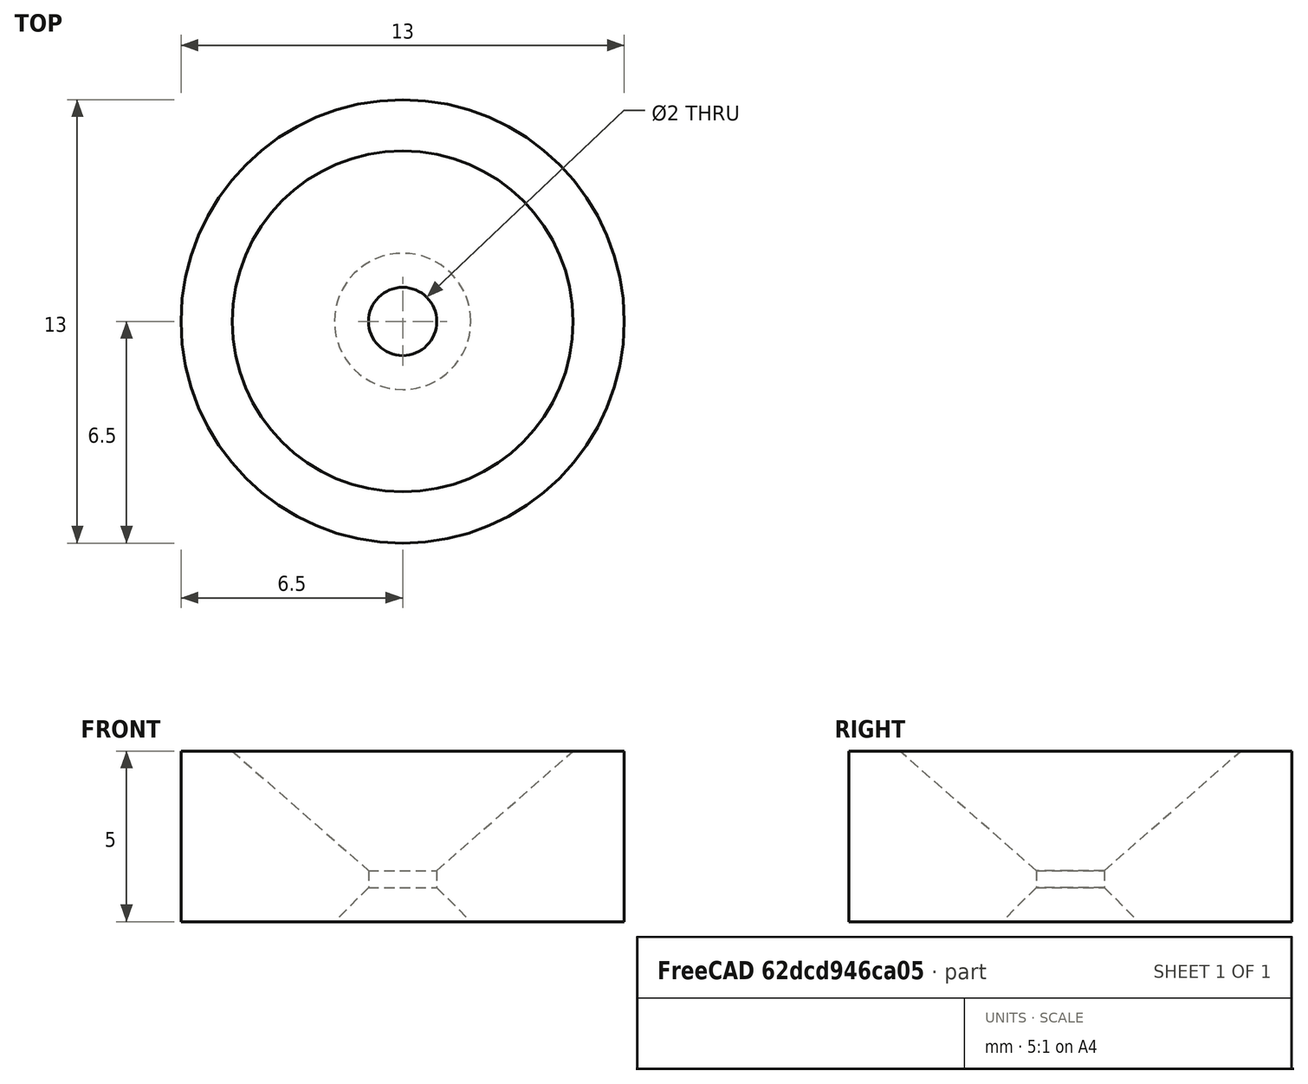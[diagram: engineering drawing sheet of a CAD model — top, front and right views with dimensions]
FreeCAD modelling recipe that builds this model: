
FCSTD DOCUMENT  (FreeCAD 0.18R16146 (Git))
Label: nozzle_big
Comment: # 2020-08-04 16:27:04: read from <userpath>/repositories/sussex_neuro/Olfactometer/hardware/mechanics/from_raiser_et_al/nozzle_big.ipt
License: All rights reserved
LicenseURL: http://en.wikipedia.org/wiki/All_rights_reserved
objects: Sketcher::SketchObject×2, Spreadsheet::Sheet×1, Part::Revolution×1
note: 3 computed .brp shape members not serialized (recipe doc carries the construction recipe); baked Part::Feature solids carry a one-line shape summary decoded from their .brp

FEATURE [Spreadsheet::Sheet] Parameters
  cells = A1=Parameter; B1=Value; C1=Fromula; D1=Tolerance; E1=Comment; A2=d11; B2(d11_)=6.5; C2=6.5mm; D2=NOMINAL; A3=d13; B3(d13_)=90; C3=90°; D3=NOMINAL; A4=d19; B4(d19_)=0.5; C4=0.5mm; D4=NOMINAL; A5=d20; B5(d20_)=2; C5=2mm; D5=NOMINAL; A6=d21; B6(d21_)=0; C6=0mm; D6=NOMINAL; A7=d22; B7(d22_)=20; C7=20mm; D7=NOMINAL; A8=d26; B8(d26_)=4.5; C8=4.5mm; D8=NOMINAL; A9=d27; B9(d27_)=0.5; C9=0.5mm; D9=NOMINAL; A10=d28; B10(d28_)=1; C10=1mm; D10=NOMINAL; A11=d29; B11(d29_)=2; C11=2mm; D11=NOMINAL; A12=d30; B12(d30_)=0.2; C12=0.2mm; D12=NOMINAL; A13=d31; B13(d31_)=1; C13=1mm; D13=NOMINAL; A14=d32; B14(d32_)=0.5; C14=0.5mm; D14=NOMINAL; A15=d33; B15(d33_)=2; C15=2mm; D15=NOMINAL; A16=d34; B16(d34_)=0; C16=0mm; D16=NOMINAL; A17=d35; B17(d35_)=20; C17=20mm; D17=NOMINAL; A18=d36; B18(d36_)=0.5; C18=0.5mm; D18=NOMINAL; A19=d37; B19(d37_)=2; C19=2mm; D19=NOMINAL; A20=d38; B20(d38_)=0; C20=0mm; D20=NOMINAL; A21=d39; B21(d39_)=20; C21=20mm; D21=NOMINAL; A22=d4; B22(d4_)=5; C22=5mm; D22=NOMINAL; A23=d5; B23(d5_)=1.5; C23=1.5mm; D23=NOMINAL
FEATURE [Sketcher::SketchObject] Sketch2
  Placement = pos=(0,0,0) rot=(0,0.707107,0.707107;3.14159rad)
  sketch-geometry (8):
    g0: LineSegment StartX=6.5 StartY=8e-16 StartZ=0 EndX=6.5 EndY=5 EndZ=0
    g1: LineSegment StartX=6.5 StartY=5 StartZ=0 EndX=5 EndY=5 EndZ=0
    g2: LineSegment StartX=6.5 StartY=5 StartZ=0 EndX=6.5 EndY=9e-16 EndZ=0
    g3: LineSegment [constr] StartX=0 StartY=-1 StartZ=0 EndX=0 EndY=6 EndZ=0
    g4: LineSegment StartX=6.5 StartY=8e-16 StartZ=0 EndX=2 EndY=8e-16 EndZ=0
    g5: LineSegment StartX=2 StartY=8e-16 StartZ=0 EndX=1 EndY=1 EndZ=0
    g6: LineSegment StartX=1 StartY=1 StartZ=0 EndX=1 EndY=1.5 EndZ=0
    g7: LineSegment StartX=5 StartY=5 StartZ=0 EndX=1 EndY=1.5 EndZ=0
  constraints (7):
    c: Perpendicular(g1,g0)
    c: Perpendicular(g3,g4)
    c: Perpendicular(g4,g6)
    c: Coincident(g0,g2)
    c: Coincident(g0,g4)
    c: Coincident(g0,g1)
    c: Coincident(g0,g2)
FEATURE [Sketcher::SketchObject] Sketch2_bp
  Placement = pos=(0,0,0) rot=(0,0.707107,0.707107;3.14159rad)
  sketch-geometry (6):
    g0: LineSegment StartX=6.5 StartY=8e-16 StartZ=0 EndX=6.5 EndY=5 EndZ=0
    g1: LineSegment StartX=6.5 StartY=5 StartZ=0 EndX=5 EndY=5 EndZ=0
    g2: LineSegment StartX=5 StartY=5 StartZ=0 EndX=1 EndY=1.5 EndZ=0
    g3: LineSegment StartX=1 StartY=1.5 StartZ=0 EndX=1 EndY=1 EndZ=0
    g4: LineSegment StartX=1 StartY=1 StartZ=0 EndX=2 EndY=8e-16 EndZ=0
    g5: LineSegment StartX=2 StartY=8e-16 StartZ=0 EndX=6.5 EndY=8e-16 EndZ=0
FEATURE [Part::Revolution] Revolution2
  Angle = 360
  Axis = (0,0,1)
  Base = (0,0,-10)
  FaceMakerClass = Part::FaceMakerBullseye
  Solid = true
  Source = -> Sketch2_bp
  Symmetric = false
